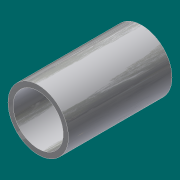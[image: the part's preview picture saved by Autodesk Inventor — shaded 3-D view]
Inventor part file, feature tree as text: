
AUTODESK INVENTOR PART (.ipt)
format: ipt  version: 2017 (Build 210142000, 142)  size: 94,208 bytes
history: native  units: in
note: dims shown in document units (in); Inventor stores cm internally (conversion verified against a paired STEP export)
features: extrude x1, sketch x1
ambient origin geometry x8: Origin, YZ Plane, XZ Plane, XY Plane, X Axis, Y Axis, Z Axis, Center Point
bodies: Solid1 (feature_tree)
feature tree (2):
  extrude  "Extrusion1"  Depth=6.0in
  sketch  "Sketch1"  dims[d0=3.5in d1=2.9in d2=6.0in d3=0.0in]
